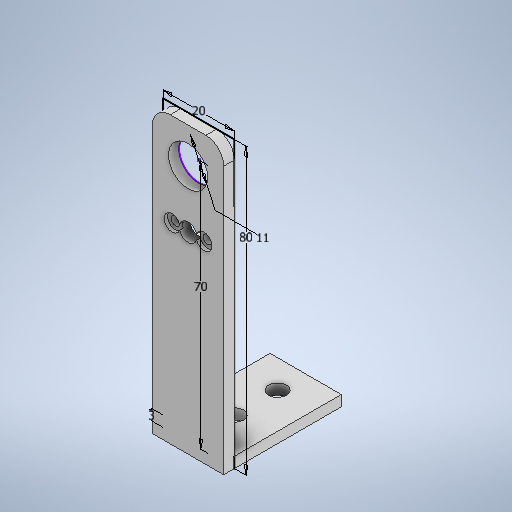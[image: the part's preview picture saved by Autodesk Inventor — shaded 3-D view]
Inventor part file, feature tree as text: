
AUTODESK INVENTOR PART (.ipt)
format: ipt  version: 2025.1 (Build 291241020, 241B)  size: 308,224 bytes
history: native  units: mm
features: extrude x8, sketch x4, fillet x1
ambient origin geometry x8: Origin, YZ Plane, XZ Plane, XY Plane, X Axis, Y Axis, Z Axis, Center Point
bodies: Solid1 (feature_tree)
feature tree (13):
  sketch  "Sketch1"  dims[d0=20.0mm d1=80.0mm d2=11.0mm]
  extrude  "Extrusion1"  Depth=80.0mm
  fillet  "Fillet1"  Radius=11.0mm
  extrude  "Extrusion2"  Depth=3.0mm TaperAngle=0.0deg
  extrude  "Extrusion3"  Depth=3.0mm
  extrude  "Extrusion4"  Depth=5.0mm
  extrude  "Extrusion5"  Depth=5.0mm
  sketch  "Sketch3"  dims[d6=5.0mm d7=3.0mm]
  extrude  "Extrusion6"  TaperAngle=0.0deg  [1 undecoded]
  extrude  "Extrusion7"  Depth=10.0mm TaperAngle=0.0deg
  extrude  "Extrusion8"  Depth=10.0mm TaperAngle=0.0deg
  sketch  "Sketch2"  dims[d3=70.0mm d4=3.0mm d5=0.0mm]
  sketch  "Sketch4"  dims[d8=30.0mm d9=0.0mm d10=5.0mm d11=5.0mm d12=0.0mm d13=0.0mm d14=10.0mm d15=0.0mm d16=10.0mm d17=0.0mm d18=5.0mm d19=16.031mm d20=4.5mm d21=4.5mm d22=4.5mm d23=4.5mm d24=1.0mm d25=0.0mm d26=0.0mm d27=0.0mm d28=2.5mm d29=2.5mm d30=0.0mm d31=0.0mm]
note: 1 required parameter value undecoded (feature->parameter linkage not recoverable at this tier; creation-order binding heuristic only, values carry confidence <= 0.55)
